# Revit family: Acoustical-Panels_Cloud-Panels_EcoScapes_Primacoustic
name_source: partatom
category: Generic Models
units: mm (PartAtom-declared; Revit-internal decimal feet)

## family parameters
Can host rebar = No
Cut with Voids When Loaded = No
Host = Face
Maintain Annotation Orientation = No
Part Type = Normal
Room Calculation Point = No
Round Connector Dimension = Use Diameter
Shared = No

## types (5) — shared parameters
CAD Details = https://www.arcat.com
Default Elevation = 48 "
Finish = PET
Keynote = 09 80 00
Manufacturer = Primacoustic
Product Page URL = https://www.arcat.com
Specification = https://www.arcat.com
Thickness = 1 "
URL = https://www.primacoustic.com

## per-type parameters (varying)
| type | Length | Width |
| EcoScapes 1x2 | 23.6 " | 11.8 " |
| EcoScapes 2x2 | 23.6 " | 23.6 " |
| EcoScapes 2x4 | 47.2 " | 23.6 " |
| EcoScapes 4x4 | 47.2 " | 47.2 " |
| EcoScapes 4x8 | 96.1 " | 48 " |

## geometry (parser evidence)
native form markers: Sweep x4
no freeform markers — native parametric forms only
